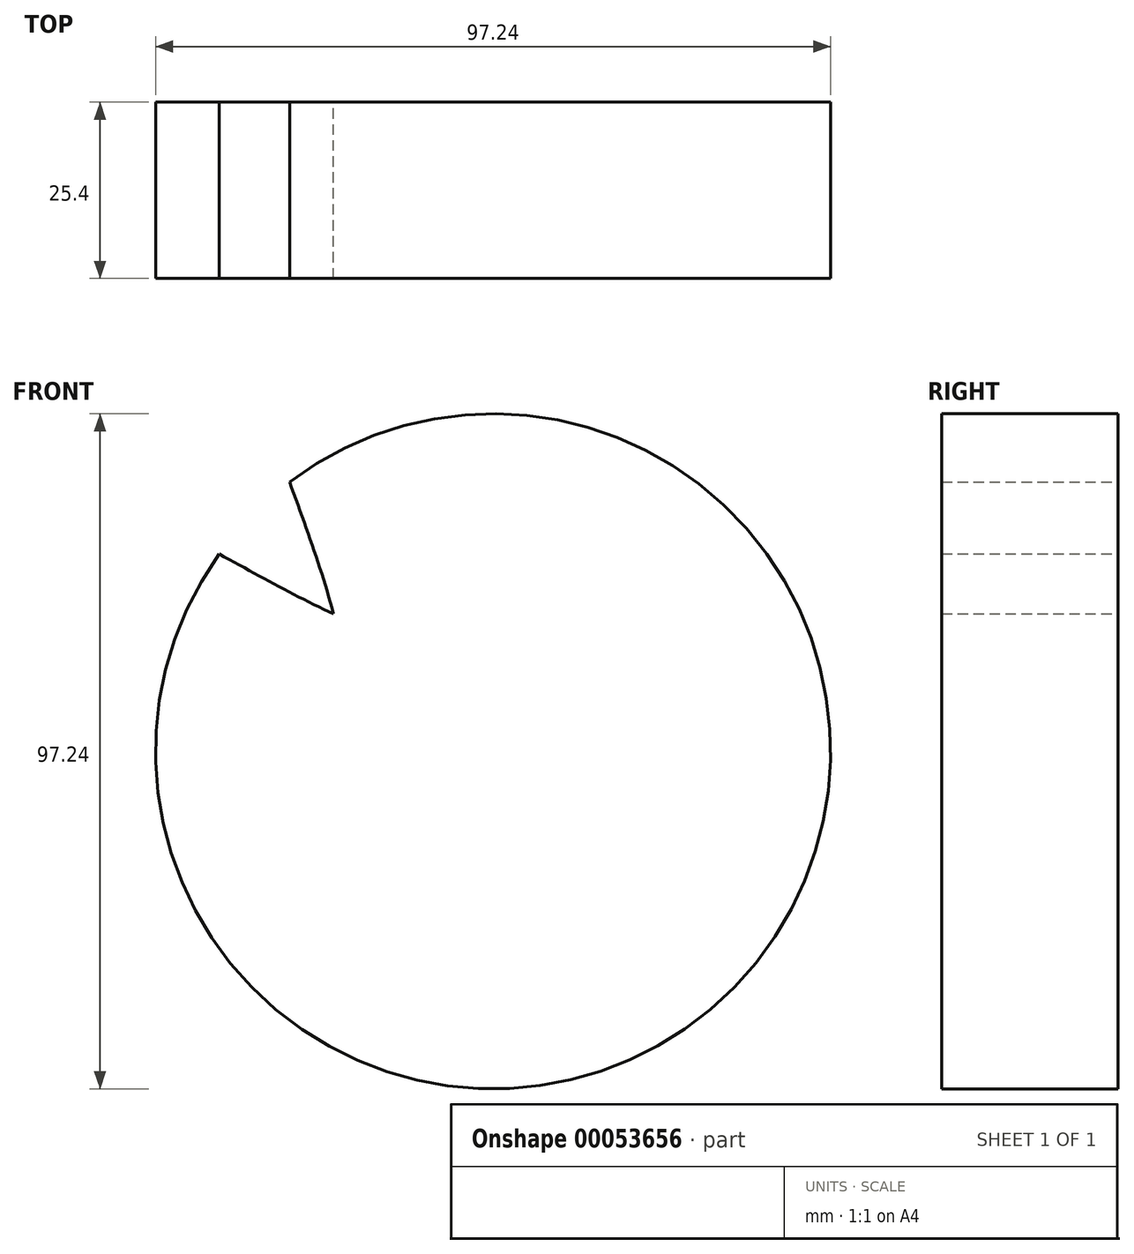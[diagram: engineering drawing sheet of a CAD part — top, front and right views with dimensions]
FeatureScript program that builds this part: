
annotation { "Feature Type Name" : "Feature", "Feature Type Description" : "" }
export const myFeature = defineFeature(function(context is Context, id is Id, definition is map)
    precondition{}
    {
        {
            var Q0;
            Q0=qCreatedBy(makeId("Front.planeOp"),FACE);
            var sketch = newSketch(context, id + "F0", { "sketchPlane" : qUnion([Q0])});
            skCircle(sketch, "E0", {"center": v(0, 0) * mm, "radius": 48.62 * mm});
            skFitSpline(sketch, "E1", {"points": [v(26.04, 41.06) * mm, v(16.9, 0) * mm, v(35.45, -33.26) * mm, v(36.26, -32.38) * mm], "startDerivative": vector(-40.45, -80.34) * mm, "endDerivative": vector(6.3, 18) * mm});
            skFitSpline(sketch, "E2", {"points": [v(-29.31, 38.78) * mm, v(-20.35, 0) * mm, v(-32.41, -36.23) * mm], "startDerivative": vector(28.3, -77.6) * mm, "endDerivative": vector(-34.72, -72.28) * mm});
            skFitSpline(sketch, "E3", {"points": [v(40.33, 27.15) * mm, v(0, 13.63) * mm, v(-39.44, 28.43) * mm], "startDerivative": vector(-80.77, -41.1) * mm, "endDerivative": vector(-78.71, 43.77) * mm});
            skFitSpline(sketch, "E4", {"points": [v(46.17, -15.23) * mm, v(0, -8.75) * mm, v(-42.1, -24.3) * mm], "startDerivative": vector(-93.03, 23.98) * mm, "endDerivative": vector(-83.4, -42.36) * mm});
            skSolve(sketch);
        }
        {
            var Q0;
            {var subQ0=sQuery(id+"F0.wireOp",EDGE,"E3");var subQ1=sQuery(id+"F0.wireOp",EDGE,"E0");var subQ2=makeQuery(id+"F0.imprint","INTERSECT",VERTEX,{"disambiguationData":[OD(0.0)],"derivedFrom":[subQ1,subQ0]});Q0=makeQuery(id+"F0.imprint","IMPRINT",FACE,{"disambiguationData":[TD([[makeQuery(id+"F0.imprint","IMPRINT",EDGE,{"disambiguationData":[TD([[subQ2,1.0]])],"derivedFrom":subQ1}),1.0]])]});}
            var Q1;
            {var subQ0=sQuery(id+"F0.wireOp",EDGE,"E2");var subQ1=sQuery(id+"F0.wireOp",EDGE,"E0");var subQ2=makeQuery(id+"F0.imprint","INTERSECT",VERTEX,{"disambiguationData":[OD(1.0)],"derivedFrom":[subQ1,subQ0]});Q1=makeQuery(id+"F0.imprint","IMPRINT",FACE,{"disambiguationData":[TD([[makeQuery(id+"F0.imprint","IMPRINT",EDGE,{"disambiguationData":[TD([[subQ2,-1.0]])],"derivedFrom":subQ1}),1.0]])]});}
            var Q2;
            {var subQ0=sQuery(id+"F0.wireOp",EDGE,"E3");var subQ1=sQuery(id+"F0.wireOp",EDGE,"E1");var subQ2=makeQuery(id+"F0.imprint","INTERSECT",VERTEX,{"derivedFrom":[subQ1,subQ0]});Q2=makeQuery(id+"F0.imprint","IMPRINT",FACE,{"disambiguationData":[TD([[makeQuery(id+"F0.imprint","IMPRINT",EDGE,{"disambiguationData":[TD([[subQ2,-1.0]])],"derivedFrom":subQ1}),-1.0]])]});}
            var Q3;
            {var subQ0=sQuery(id+"F0.wireOp",EDGE,"E3");var subQ1=sQuery(id+"F0.wireOp",EDGE,"E0");var subQ2=makeQuery(id+"F0.imprint","INTERSECT",VERTEX,{"disambiguationData":[OD(1.0)],"derivedFrom":[subQ1,subQ0]});Q3=makeQuery(id+"F0.imprint","IMPRINT",FACE,{"disambiguationData":[TD([[makeQuery(id+"F0.imprint","IMPRINT",EDGE,{"disambiguationData":[TD([[subQ2,-1.0]])],"derivedFrom":subQ1}),1.0]])]});}
            var Q4;
            {var subQ0=sQuery(id+"F0.wireOp",EDGE,"E1");var subQ1=sQuery(id+"F0.wireOp",EDGE,"E0");var subQ2=makeQuery(id+"F0.imprint","INTERSECT",VERTEX,{"disambiguationData":[OD(0.0)],"derivedFrom":[subQ1,subQ0]});Q4=makeQuery(id+"F0.imprint","IMPRINT",FACE,{"disambiguationData":[TD([[makeQuery(id+"F0.imprint","IMPRINT",EDGE,{"disambiguationData":[TD([[subQ2,1.0]])],"derivedFrom":subQ1}),1.0]])]});}
            var Q5;
            {var subQ0=sQuery(id+"F0.wireOp",EDGE,"E1");var subQ1=sQuery(id+"F0.wireOp",EDGE,"E0");var subQ2=makeQuery(id+"F0.imprint","INTERSECT",VERTEX,{"disambiguationData":[OD(0.0)],"derivedFrom":[subQ1,subQ0]});Q5=makeQuery(id+"F0.imprint","IMPRINT",FACE,{"disambiguationData":[TD([[makeQuery(id+"F0.imprint","IMPRINT",EDGE,{"disambiguationData":[TD([[subQ2,-1.0]])],"derivedFrom":subQ1}),1.0]])]});}
            var Q6;
            {var subQ0=sQuery(id+"F0.wireOp",EDGE,"E2");var subQ1=sQuery(id+"F0.wireOp",EDGE,"E0");var subQ2=makeQuery(id+"F0.imprint","INTERSECT",VERTEX,{"disambiguationData":[OD(1.0)],"derivedFrom":[subQ1,subQ0]});Q6=makeQuery(id+"F0.imprint","IMPRINT",FACE,{"disambiguationData":[TD([[makeQuery(id+"F0.imprint","IMPRINT",EDGE,{"disambiguationData":[TD([[subQ2,1.0]])],"derivedFrom":subQ1}),1.0]])]});}
            var Q7;
            {var subQ0=sQuery(id+"F0.wireOp",EDGE,"E1");var subQ1=sQuery(id+"F0.wireOp",EDGE,"E0");var subQ2=makeQuery(id+"F0.imprint","INTERSECT",VERTEX,{"disambiguationData":[OD(1.0)],"derivedFrom":[subQ1,subQ0]});Q7=makeQuery(id+"F0.imprint","IMPRINT",FACE,{"disambiguationData":[TD([[makeQuery(id+"F0.imprint","IMPRINT",EDGE,{"disambiguationData":[TD([[subQ2,1.0]])],"derivedFrom":subQ1}),1.0]])]});}
            extrude(context, id + "F1", {"entities" : qUnion([Q0, Q1, Q2, Q3, Q4, Q5, Q6, Q7]), "depth" : 25.4 * mm});
        }
    });
